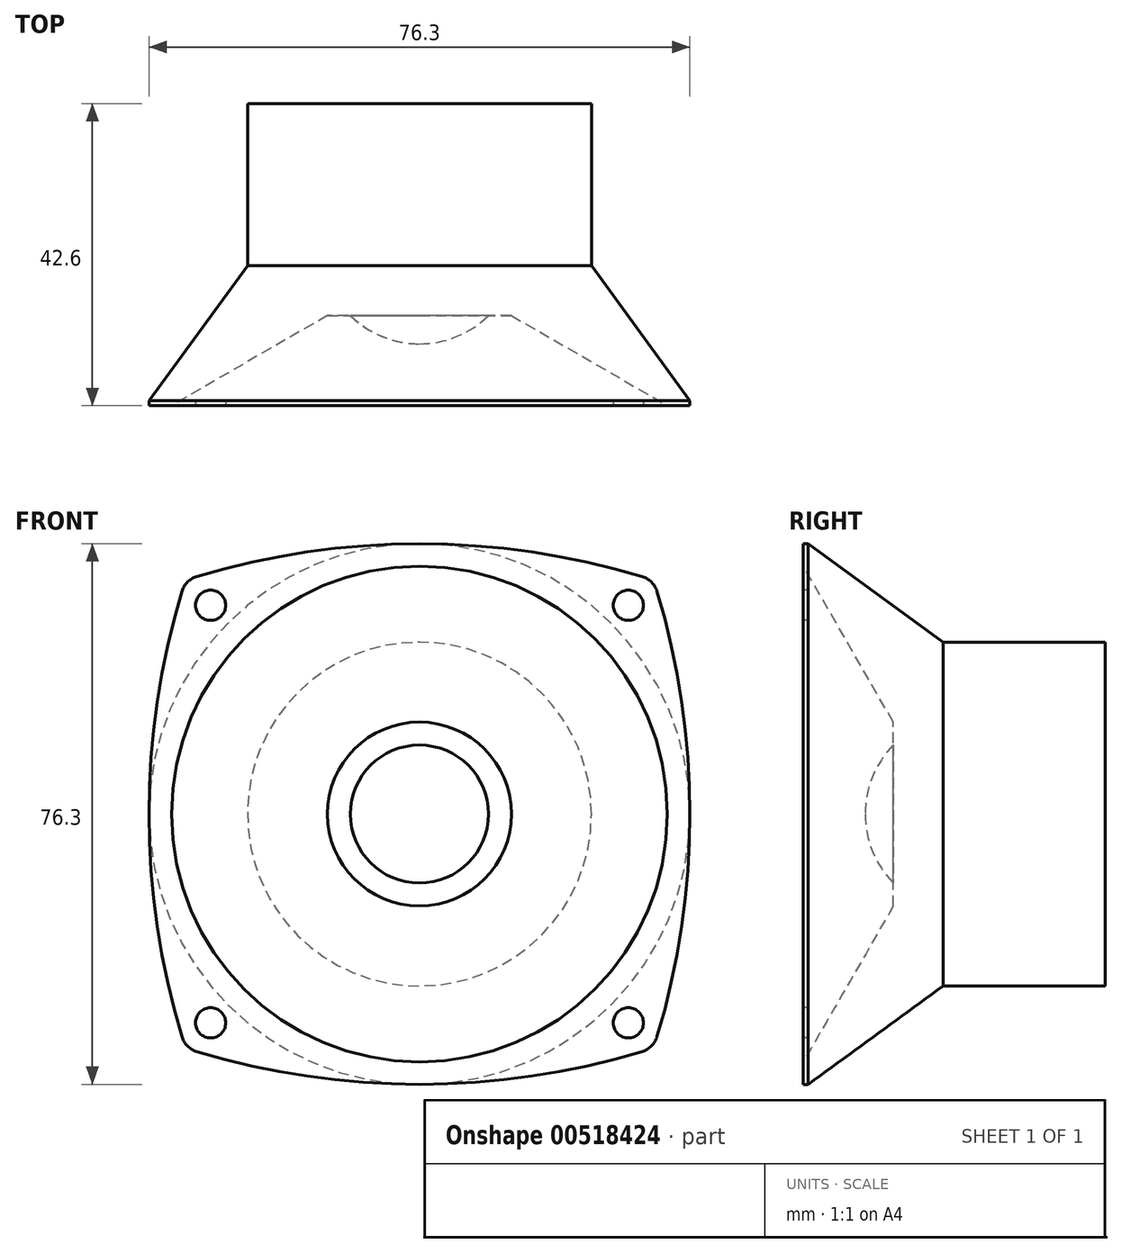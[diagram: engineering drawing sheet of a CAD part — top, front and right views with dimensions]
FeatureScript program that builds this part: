
annotation { "Feature Type Name" : "Feature", "Feature Type Description" : "" }
export const myFeature = defineFeature(function(context is Context, id is Id, definition is map)
    precondition{}
    {
        {
            var Q0;
            Q0=qCreatedBy(makeId("Front.planeOp"),FACE);
            var sketch = newSketch(context, id + "F0", { "sketchPlane" : qUnion([Q0])});
            skCircle(sketch, "E0", {"center": v(0, 0) * mm, "radius": 24.26 * mm});
            skSolve(sketch);
        }
        {
            var Q0;
            Q0 = qSketchRegion(id + "F0", true);
            extrude(context, id + "F1", {"entities" : qUnion([Q0]), "depth" : 22.86 * mm, "offsetDistance" : 25.4 * mm});
        }
        {
            var Q0;
            Q0=makeQuery(id+"F1.opExtrude","CAP_FACE",FACE,{"disambiguationData":[OSD([sQuery(id+"F0.wireOp",EDGE,"E0")])],"isStart":false});
            var sketch = newSketch(context, id + "F2", { "sketchPlane" : qUnion([Q0])});
            skCircle(sketch, "E1.0.0", {"center": v(0, 0) * mm, "radius": 24.26 * mm});
            skSolve(sketch);
        }
        {
            var Q0;
            Q0 = qSketchRegion(id + "F2", true);
            extrude(context, id + "F3", {"entities" : qUnion([Q0]), "operationType" : NewBodyOperationType.ADD, "depth" : 19.05 * mm, "offsetDistance" : 25.4 * mm, "hasDraft" : true, "draftAngle" : 36.1 * degree});
        }
        {
            var Q0;
            Q0=makeQuery(id+"F3.opExtrude","CAP_FACE",FACE,{"disambiguationData":[OSD([sQuery(id+"F2.wireOp",EDGE,"E1.0.0")])],"isStart":false});
            var sketch = newSketch(context, id + "F4", { "sketchPlane" : qUnion([Q0])});
            skLineSegment(sketch, "E2.bottom", {"start": v(33.02, -33.02) * mm, "end": v(-33.02, -33.02) * mm, "construction": true});
            skLineSegment(sketch, "E2.top", {"start": v(33.02, 33.02) * mm, "end": v(-33.02, 33.02) * mm, "construction": true});
            skLineSegment(sketch, "E2.left", {"start": v(33.02, -33.02) * mm, "end": v(33.02, 33.02) * mm, "construction": true});
            skLineSegment(sketch, "E2.right", {"start": v(-33.02, -33.02) * mm, "end": v(-33.02, 33.02) * mm, "construction": true});
            skPoint(sketch, "E2.middle", {"position": v(0, 0) * mm});
            skArc(sketch, "E3", {"start": v(31.4, 33.52) * mm, "mid": v(0, 38.15) * mm, "end": v(-31.4, 33.52) * mm});
            skArc(sketch, "E4", {"start": v(-31.4, -33.52) * mm, "mid": v(0, -38.15) * mm, "end": v(31.4, -33.52) * mm});
            skArc(sketch, "E5", {"start": v(-33.52, 31.4) * mm, "mid": v(-38.15, 0) * mm, "end": v(-33.52, -31.4) * mm});
            skArc(sketch, "E6", {"start": v(33.52, -31.4) * mm, "mid": v(38.15, 0) * mm, "end": v(33.52, 31.4) * mm});
            skPoint(sketch, "E7.visualSharp", {"position": v(-33.02, 33.02) * mm});
            skArc(sketch, "E7.filletArc", {"start": v(-31.4, 33.52) * mm, "mid": v(-32.73, 32.73) * mm, "end": v(-33.52, 31.4) * mm});
            skPoint(sketch, "E8.visualSharp", {"position": v(33.02, 33.02) * mm});
            skArc(sketch, "E8.filletArc", {"start": v(33.52, 31.4) * mm, "mid": v(32.73, 32.73) * mm, "end": v(31.4, 33.52) * mm});
            skPoint(sketch, "E9.visualSharp", {"position": v(33.02, -33.02) * mm});
            skArc(sketch, "E9.filletArc", {"start": v(31.4, -33.52) * mm, "mid": v(32.73, -32.73) * mm, "end": v(33.52, -31.4) * mm});
            skPoint(sketch, "E10.visualSharp", {"position": v(-33.02, -33.02) * mm});
            skArc(sketch, "E10.filletArc", {"start": v(-33.52, -31.4) * mm, "mid": v(-32.73, -32.73) * mm, "end": v(-31.4, -33.52) * mm});
            skSolve(sketch);
        }
        {
            var Q0;
            Q0 = qSketchRegion(id + "F4", true);
            extrude(context, id + "F5", {"entities" : qUnion([Q0]), "operationType" : NewBodyOperationType.ADD, "depth" : 0.69 * mm, "offsetDistance" : 25.4 * mm});
        }
        {
            var Q0;
            Q0=makeQuery(id+"F5.opExtrude","CAP_FACE",FACE,{"disambiguationData":[OSD([sQuery(id+"F4.wireOp",EDGE,"E3"),sQuery(id+"F4.wireOp",EDGE,"E4"),sQuery(id+"F4.wireOp",EDGE,"E5"),sQuery(id+"F4.wireOp",EDGE,"E6")])],"isStart":false});
            var sketch = newSketch(context, id + "F6", { "sketchPlane" : qUnion([Q0])});
            skCircle(sketch, "E11.0", {"center": v(0, 0) * mm, "radius": 34.97 * mm});
            skSolve(sketch);
        }
        {
            var Q0;
            Q0 = qSketchRegion(id + "F6", true);
            extrude(context, id + "F7", {"entities" : qUnion([Q0]), "operationType" : NewBodyOperationType.REMOVE, "oppositeDirection" : true, "depth" : 12.7 * mm, "offsetDistance" : 25.4 * mm, "hasDraft" : true, "draftAngle" : 60 * degree, "draftPullDirection" : true});
        }
        {
            var Q0;
            Q0=makeQuery(id+"F5.opExtrude","CAP_FACE",FACE,{"disambiguationData":[OSD([sQuery(id+"F4.wireOp",EDGE,"E3"),sQuery(id+"F4.wireOp",EDGE,"E4"),sQuery(id+"F4.wireOp",EDGE,"E5"),sQuery(id+"F4.wireOp",EDGE,"E6")])],"isStart":false});
            var sketch = newSketch(context, id + "F8", { "sketchPlane" : qUnion([Q0])});
            skLineSegment(sketch, "E12.bottom", {"start": v(29.46, -29.46) * mm, "end": v(-29.46, -29.46) * mm, "construction": true});
            skLineSegment(sketch, "E12.top", {"start": v(29.46, 29.46) * mm, "end": v(-29.46, 29.46) * mm, "construction": true});
            skLineSegment(sketch, "E12.left", {"start": v(29.46, -29.46) * mm, "end": v(29.46, 29.46) * mm, "construction": true});
            skLineSegment(sketch, "E12.right", {"start": v(-29.46, -29.46) * mm, "end": v(-29.46, 29.46) * mm, "construction": true});
            skPoint(sketch, "E12.middle", {"position": v(0, 0) * mm});
            skCircle(sketch, "E13", {"center": v(-29.46, 29.46) * mm, "radius": 2.13 * mm});
            skCircle(sketch, "E14", {"center": v(29.46, 29.46) * mm, "radius": 2.13 * mm});
            skCircle(sketch, "E15", {"center": v(-29.46, -29.46) * mm, "radius": 2.13 * mm});
            skCircle(sketch, "E16", {"center": v(29.46, -29.46) * mm, "radius": 2.13 * mm});
            skSolve(sketch);
        }
        {
            var Q0;
            Q0 = qSketchRegion(id + "F8", true);
            extrude(context, id + "F9", {"entities" : qUnion([Q0]), "operationType" : NewBodyOperationType.REMOVE, "endBound" : BoundingType.THROUGH_ALL, "oppositeDirection" : true, "depth" : 25.4 * mm, "offsetDistance" : 25.4 * mm});
        }
        {
            var Q0;
            Q0=qCreatedBy(makeId("Top.planeOp"),FACE);
            var sketch = newSketch(context, id + "F10", { "sketchPlane" : qUnion([Q0])});
            skArc(sketch, "E17", {"start": v(0, -33.89) * mm, "mid": v(5.9, -32.57) * mm, "end": v(10.68, -28.87) * mm});
            skLineSegment(sketch, "E18", {"start": v(0, -33.89) * mm, "end": v(0, -20.01) * mm});
            skLineSegment(sketch, "E19", {"start": v(10.68, -28.87) * mm, "end": v(0, -20.01) * mm});
            skSolve(sketch);
        }
        {
            var Q0;
            Q0 = qSketchRegion(id + "F10", true);
            var Q1;
            Q1=sQuery(id+"F10.wireOp",EDGE,"E18");
            revolve(context, id + "F11", {"operationType" : NewBodyOperationType.ADD, "entities" : qUnion([Q0]), "axis" : qUnion([Q1]), "revolveType" : RevolveType.FULL});
        }
    });
